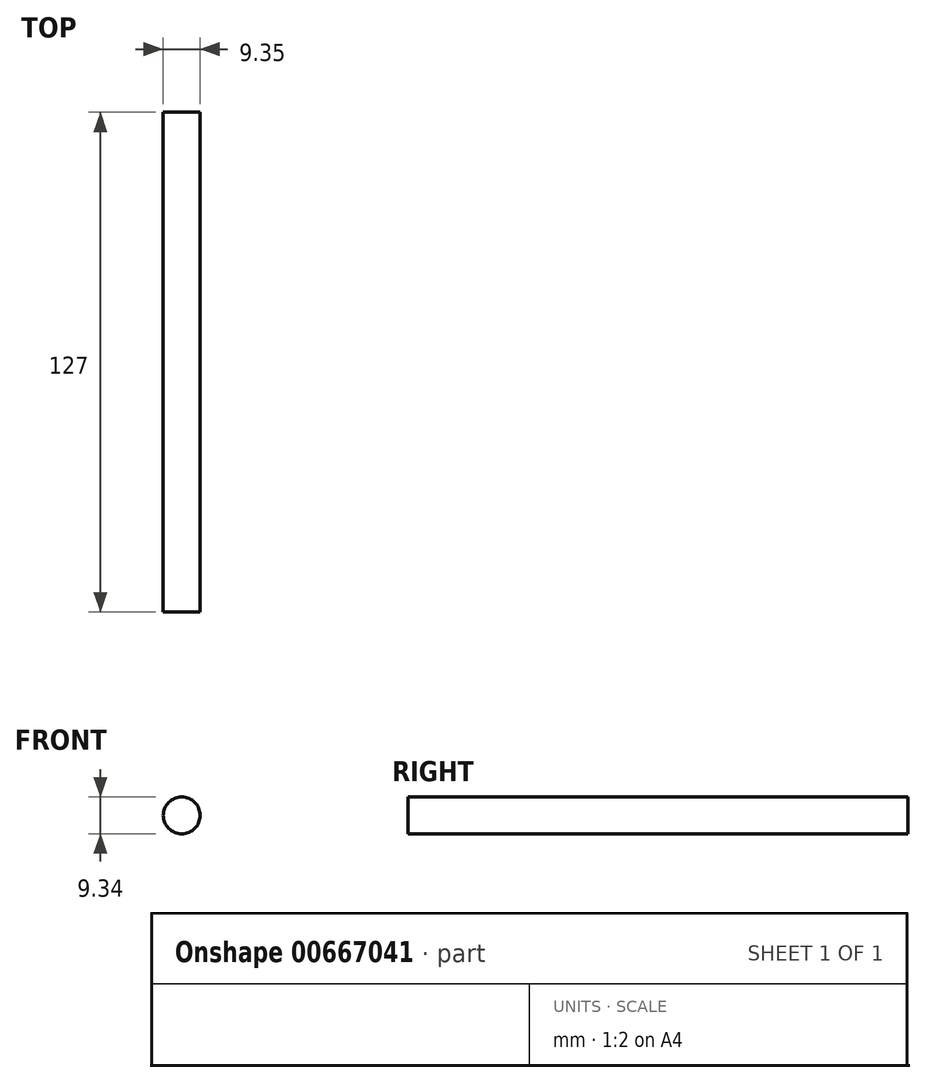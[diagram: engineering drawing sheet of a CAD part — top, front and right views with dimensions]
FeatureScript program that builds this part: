
annotation { "Feature Type Name" : "Feature", "Feature Type Description" : "" }
export const myFeature = defineFeature(function(context is Context, id is Id, definition is map)
    precondition{}
    {
        {
            var Q0;
            Q0=qCreatedBy(makeId("Front.planeOp"),FACE);
            var sketch = newSketch(context, id + "F0", { "sketchPlane" : qUnion([Q0])});
            skCircle(sketch, "E0", {"center": v(108.12, 0) * mm, "radius": 4.67 * mm});
            skSolve(sketch);
        }
        {
            var Q0;
            Q0 = qSketchRegion(id + "F0", true);
            extrude(context, id + "F1", {"entities" : qUnion([Q0]), "depth" : 127 * mm, "offsetDistance" : 25.4 * mm});
        }
    });
